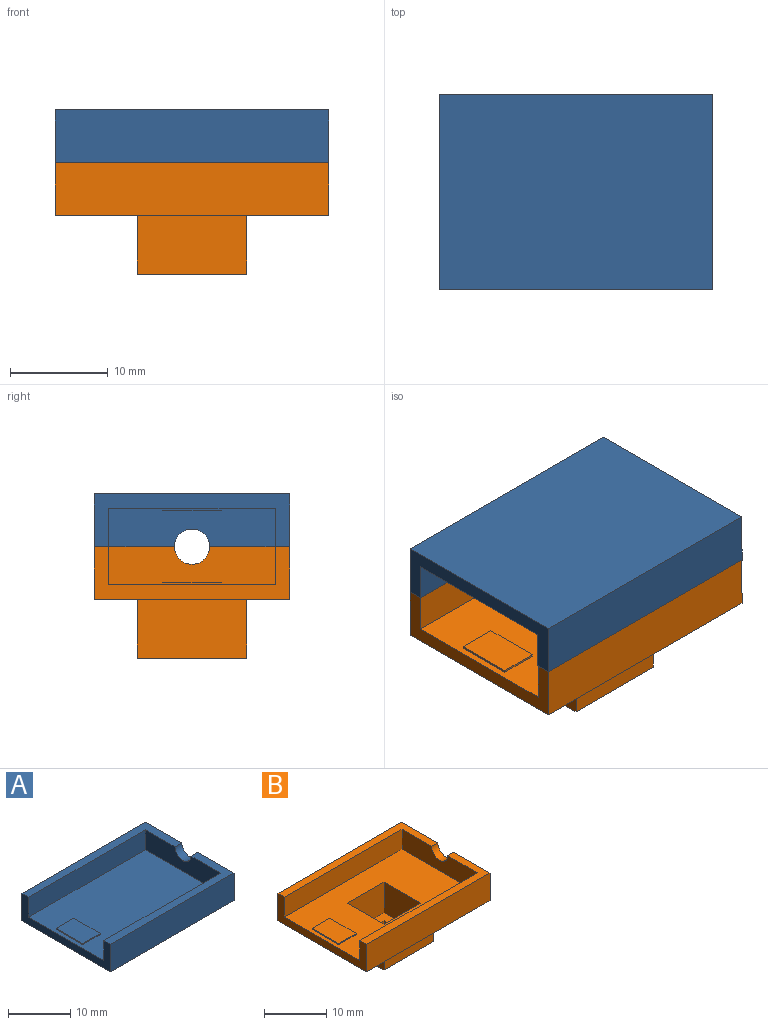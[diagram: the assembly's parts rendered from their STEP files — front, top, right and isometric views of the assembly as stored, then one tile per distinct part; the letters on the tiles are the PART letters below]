
ASSEMBLY  parts=2 mates=1
PART A: 17 faces, bbox 28x20x5.4 mm
  f0: plane 28x8.2mm, normal (0,0,1), area 52.6mm2, adj f1,f2,f5,f6,f13,f16
  f1: plane 20x5.4mm, normal (1,0,0), area 102.9mm2, adj f0,f4,f5,f7,f15,f16
  f2: plane 16.99x3.9mm, normal (-1,0,0), area 61.2mm2, adj f0,f3,f13,f14,f15,f16
  f3: plane 26.45x16.99mm, normal (0,0,1), area 425.5mm2, adj f2,f6,f8,f9,f10,f11,f13,f14
  f4: plane 28x5.4mm, normal (0,-1,0), area 151.2mm2, adj f1,f6,f7,f15
  f5: plane 28x5.4mm, normal (0,1,0), area 151.2mm2, adj f0,f1,f6,f7
  f6: plane 20x5.4mm, normal (-1,0,0), area 41.7mm2, adj f0,f3,f4,f5,f7,f13,f14,f15
  f7: plane 28x20mm, normal (0,0,-1), area 560mm2, adj f1,f4,f5,f6
  f8: plane 6x0.2mm, normal (1,0,0), area 1.2mm2, adj f3,f9,f11,f12
  f9: plane 4x0.2mm, normal (0,1,0), area 0.8mm2, adj f3,f8,f10,f12
  f10: plane 6x0.2mm, normal (-1,0,0), area 1.2mm2, adj f3,f9,f11,f12
  f11: plane 4x0.2mm, normal (0,-1,0), area 0.8mm2, adj f3,f8,f10,f12
  f12: plane 6x4mm, normal (0,0,1), area 24mm2, adj f8,f9,f10,f11
  f13: plane 26.45x3.9mm, normal (0,-1,0), area 103.2mm2, adj f0,f2,f3,f6
  f14: plane 26.45x3.9mm, normal (0,1,0), area 103.2mm2, adj f2,f3,f6,f15
  f15: plane 28x8.2mm, normal (0,0,1), area 52.4mm2, adj f1,f2,f4,f6,f14,f16
  f16: cylinder r=1.8mm len=3.6mm, axis (1,0,0), area 8.7mm2, adj f0,f1,f2,f15
PART B: 31 faces, bbox 28x20x11.4 mm
  f0: plane 28x8.2mm, normal (0,0,1), area 50.4mm2, adj f1,f2,f19,f20,f27,f30
  f1: plane 20x5.4mm, normal (1,0,0), area 102.9mm2, adj f0,f18,f19,f21,f29,f30
  f2: plane 17.05x3.9mm, normal (-1,0,0), area 61.4mm2, adj f0,f3,f27,f28,f29,f30
  f3: plane 26.61x17.05mm, normal (0,0,1), area 362.4mm2, adj f2,f14,f15,f16,f17,f20,f22,f23
  f4: plane 8.2x8.2mm, normal (0,0,1), area 42.2mm2, adj f8,f9,f10,f11,f14,f15,f16,f17
  f5: plane 11.2x6mm, normal (0,-1,0), area 67.2mm2, adj f6,f12,f13,f21
  f6: plane 11.2x6mm, normal (1,0,0), area 67.2mm2, adj f5,f7,f13,f21
  f7: plane 11.2x6mm, normal (0,1,0), area 67.2mm2, adj f6,f12,f13,f21
  f8: plane 5x1.5mm, normal (-1,0,0), area 7.5mm2, adj f4,f9,f11,f13
  f9: plane 5x1.5mm, normal (0,1,0), area 7.5mm2, adj f4,f8,f10,f13
  f10: plane 5x1.5mm, normal (1,0,0), area 7.5mm2, adj f4,f9,f11,f13
  f11: plane 5x1.5mm, normal (0,-1,0), area 7.5mm2, adj f4,f8,f10,f13
  f12: plane 11.2x6mm, normal (-1,0,0), area 67.2mm2, adj f5,f7,f13,f21
  f13: plane 11.2x11.2mm, normal (0,0,-1), area 100.4mm2, adj f5,f6,f7,f8,f9,f10,f11,f12
  f14: plane 8.2x6mm, normal (-1,0,0), area 49.2mm2, adj f3,f4,f15,f17
  f15: plane 8.2x6mm, normal (0,1,0), area 49.2mm2, adj f3,f4,f14,f16
  f16: plane 8.2x6mm, normal (1,0,0), area 49.2mm2, adj f3,f4,f15,f17
  f17: plane 8.2x6mm, normal (0,-1,0), area 49.2mm2, adj f3,f4,f14,f16
  f18: plane 28x5.4mm, normal (0,-1,0), area 151.2mm2, adj f1,f20,f21,f29
  f19: plane 28x5.4mm, normal (0,1,0), area 151.2mm2, adj f0,f1,f20,f21
  f20: plane 20x5.4mm, normal (-1,0,0), area 41.5mm2, adj f0,f3,f18,f19,f21,f27,f28,f29
  f21: plane 28x20mm, normal (0,0,-1), area 434.6mm2, adj f1,f5,f6,f7,f12,f18,f19,f20
  f22: plane 6x0.2mm, normal (1,0,0), area 1.2mm2, adj f3,f23,f25,f26
  f23: plane 4x0.2mm, normal (0,1,0), area 0.8mm2, adj f3,f22,f24,f26
  f24: plane 6x0.2mm, normal (-1,0,0), area 1.2mm2, adj f3,f23,f25,f26
  f25: plane 4x0.2mm, normal (0,-1,0), area 0.8mm2, adj f3,f22,f24,f26
  f26: plane 6x4mm, normal (0,0,1), area 24mm2, adj f22,f23,f24,f25
  f27: plane 26.61x3.9mm, normal (0,-1,0), area 103.8mm2, adj f0,f2,f3,f20
  f28: plane 26.61x3.9mm, normal (0,1,0), area 103.8mm2, adj f2,f3,f20,f29
  f29: plane 28x8.2mm, normal (0,0,1), area 50.9mm2, adj f1,f2,f18,f20,f28,f30
  f30: cylinder r=1.8mm len=3.6mm, axis (1,0,0), area 7.9mm2, adj f0,f1,f2,f29
PLACE A rot(axis=(1,0,0),180deg) t=(-13.92,-0.9,11.59)mm
PLACE B t=(-13.92,-0.9,-5.21)mm
MATE fastened A.f1 <-> B.f1  axis (1,0,0) through (0.08,-6.8,6.19)mm
